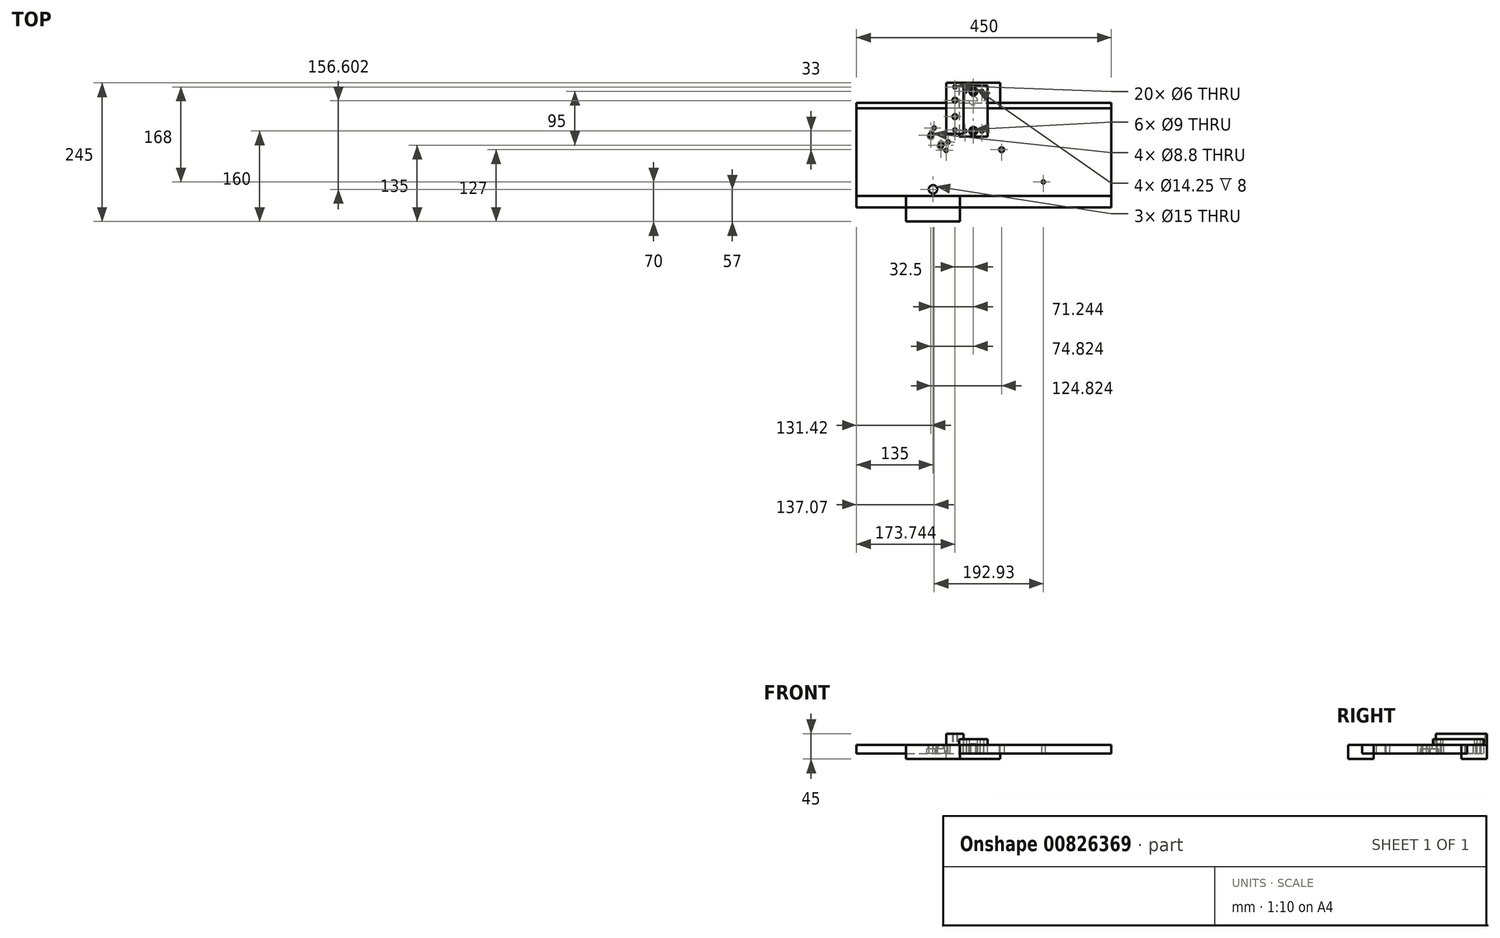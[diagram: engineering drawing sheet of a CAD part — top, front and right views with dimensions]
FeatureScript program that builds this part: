
annotation { "Feature Type Name" : "Feature", "Feature Type Description" : "" }
export const myFeature = defineFeature(function(context is Context, id is Id, definition is map)
    precondition{}
    {
        {
            var Q0;
            Q0=qCreatedBy(makeId("Top.planeOp"),FACE);
            var sketch = newSketch(context, id + "F0", { "sketchPlane" : qUnion([Q0])});
            skLineSegment(sketch, "E0.bottom", {"start": v(120, -25) * mm, "end": v(-330, -25) * mm});
            skLineSegment(sketch, "E0.top", {"start": v(120, 130) * mm, "end": v(-330, 130) * mm});
            skLineSegment(sketch, "E0.left", {"start": v(120, -25) * mm, "end": v(120, 130) * mm});
            skLineSegment(sketch, "E0.right", {"start": v(-330, -25) * mm, "end": v(-330, 130) * mm});
            skSolve(sketch);
        }
        {
            var Q0;
            Q0=makeQuery(id+"F0.imprint","IMPRINT",FACE,{"disambiguationData":[TD([[makeQuery(id+"F0.imprint","IMPRINT",EDGE,{"derivedFrom":sQuery(id+"F0.wireOp",EDGE,"E0.bottom")}),-1.0]])]});
            extrude(context, id + "F1", {"entities" : qUnion([Q0]), "oppositeDirection" : true, "depth" : 15 * mm, "offsetDistance" : 25 * mm});
        }
        {
            var Q0;
            Q0=makeQuery(id+"F1.opExtrude","CAP_FACE",FACE,{"disambiguationData":[OSD([sQuery(id+"F0.wireOp",EDGE,"E0.bottom"),sQuery(id+"F0.wireOp",EDGE,"E0.top"),sQuery(id+"F0.wireOp",EDGE,"E0.left"),sQuery(id+"F0.wireOp",EDGE,"E0.right")])],"isStart":true});
            var sketch = newSketch(context, id + "F2", { "sketchPlane" : qUnion([Q0])});
            skLineSegment(sketch, "E1.bottom", {"start": v(-330, -25) * mm, "end": v(120, -25) * mm});
            skLineSegment(sketch, "E1.top", {"start": v(-330, -45) * mm, "end": v(120, -45) * mm});
            skLineSegment(sketch, "E1.left", {"start": v(-330, -25) * mm, "end": v(-330, -45) * mm});
            skLineSegment(sketch, "E1.right", {"start": v(120, -25) * mm, "end": v(120, -45) * mm});
            skLineSegment(sketch, "E2.bottom", {"start": v(-330, 130) * mm, "end": v(120, 130) * mm});
            skLineSegment(sketch, "E2.top", {"start": v(-330, 140) * mm, "end": v(120, 140) * mm});
            skLineSegment(sketch, "E2.left", {"start": v(-330, 130) * mm, "end": v(-330, 140) * mm});
            skLineSegment(sketch, "E2.right", {"start": v(120, 130) * mm, "end": v(120, 140) * mm});
            skSolve(sketch);
        }
        {
            var Q0;
            Q0=makeQuery(id+"F2.imprint","IMPRINT",FACE,{"disambiguationData":[TD([[makeQuery(id+"F2.imprint","IMPRINT",EDGE,{"derivedFrom":sQuery(id+"F2.wireOp",EDGE,"E1.bottom")}),-1.0]])]});
            var sketch = newSketch(context, id + "F3", { "sketchPlane" : qUnion([Q0])});
            skLineSegment(sketch, "E3.bottom", {"start": v(-242.5, -25) * mm, "end": v(-147.5, -25) * mm});
            skLineSegment(sketch, "E3.top", {"start": v(-242.5, -70) * mm, "end": v(-147.5, -70) * mm});
            skLineSegment(sketch, "E3.left", {"start": v(-242.5, -25) * mm, "end": v(-242.5, -70) * mm});
            skLineSegment(sketch, "E3.right", {"start": v(-147.5, -25) * mm, "end": v(-147.5, -70) * mm});
            skLineSegment(sketch, "E4", {"start": v(-195, -23) * mm, "end": v(-73.76, 47) * mm});
            skLineSegment(sketch, "E5", {"start": v(-123.76, 133.6) * mm, "end": v(-73.76, 47) * mm});
            skSolve(sketch);
        }
        {
            var Q0;
            Q0=makeQuery(id+"F3.imprint","IMPRINT",FACE,{"disambiguationData":[TD([[makeQuery(id+"F3.imprint","IMPRINT",EDGE,{"derivedFrom":makeQuery(id+"F2.imprint","IMPRINT",EDGE,{"derivedFrom":sQuery(id+"F2.wireOp",EDGE,"E2.bottom")})}),1.0]])]});
            var sketch = newSketch(context, id + "F4", { "sketchPlane" : qUnion([Q0])});
            skLineSegment(sketch, "E6.bottom", {"start": v(-242.5, -70) * mm, "end": v(-147.5, -70) * mm});
            skLineSegment(sketch, "E6.top", {"start": v(-242.5, -25) * mm, "end": v(-147.5, -25) * mm});
            skLineSegment(sketch, "E6.left", {"start": v(-242.5, -70) * mm, "end": v(-242.5, -25) * mm});
            skLineSegment(sketch, "E6.right", {"start": v(-147.5, -70) * mm, "end": v(-147.5, -25) * mm});
            skLineSegment(sketch, "E7.bottom", {"start": v(-171.26, 130) * mm, "end": v(-76.26, 130) * mm});
            skLineSegment(sketch, "E7.top", {"start": v(-171.26, 175) * mm, "end": v(-76.26, 175) * mm});
            skLineSegment(sketch, "E7.left", {"start": v(-171.26, 130) * mm, "end": v(-171.26, 175) * mm});
            skLineSegment(sketch, "E7.right", {"start": v(-76.26, 130) * mm, "end": v(-76.26, 175) * mm});
            skSolve(sketch);
        }
        {
            var Q0;
            Q0 = qSketchRegion(id + "F4", true);
            extrude(context, id + "F5", {"entities" : qUnion([Q0]), "oppositeDirection" : true, "depth" : 25 * mm, "offsetDistance" : 25 * mm});
        }
        {
            var Q0;
            Q0=makeQuery(id+"F5.opExtrude","CAP_FACE",FACE,{"disambiguationData":[OSD([sQuery(id+"F4.wireOp",EDGE,"E7.bottom"),sQuery(id+"F4.wireOp",EDGE,"E7.top"),sQuery(id+"F4.wireOp",EDGE,"E7.left"),sQuery(id+"F4.wireOp",EDGE,"E7.right")])],"isStart":true});
            var sketch = newSketch(context, id + "F6", { "sketchPlane" : qUnion([Q0])});
            skLineSegment(sketch, "E8.bottom", {"start": v(-171.26, 175) * mm, "end": v(-141.26, 175) * mm});
            skLineSegment(sketch, "E8.top", {"start": v(-171.26, 85) * mm, "end": v(-141.26, 85) * mm});
            skLineSegment(sketch, "E8.left", {"start": v(-171.26, 175) * mm, "end": v(-171.26, 85) * mm});
            skLineSegment(sketch, "E8.right", {"start": v(-141.26, 175) * mm, "end": v(-141.26, 85) * mm});
            skCircle(sketch, "E9", {"center": v(-156.26, 168) * mm, "radius": 3 * mm});
            skCircle(sketch, "E10", {"center": v(-156.26, 144.5) * mm, "radius": 4.5 * mm});
            skCircle(sketch, "E11", {"center": v(-156.26, 115.5) * mm, "radius": 4.5 * mm});
            skCircle(sketch, "E12", {"center": v(-156.26, 92) * mm, "radius": 3 * mm});
            skLineSegment(sketch, "E13", {"start": v(-156.26, 168) * mm, "end": v(-156.26, 144.5) * mm});
            skLineSegment(sketch, "E14", {"start": v(-156.26, 115.5) * mm, "end": v(-156.26, 92) * mm});
            skLineSegment(sketch, "E15", {"start": v(-156.26, 115.5) * mm, "end": v(-156.26, 144.5) * mm});
            skPoint(sketch, "E16", {"position": v(-156.26, 175) * mm});
            skLineSegment(sketch, "E17", {"start": v(-91.26, 168) * mm, "end": v(-91.26, 144.5) * mm});
            skLineSegment(sketch, "E18", {"start": v(-91.26, 144.5) * mm, "end": v(-91.26, 115.5) * mm});
            skLineSegment(sketch, "E19", {"start": v(-91.26, 115.5) * mm, "end": v(-91.26, 92) * mm});
            skLineSegment(sketch, "E20", {"start": v(-156.26, 168) * mm, "end": v(-91.26, 168) * mm});
            skLineSegment(sketch, "E21", {"start": v(-162.5, -63) * mm, "end": v(-162.5, -39.5) * mm});
            skLineSegment(sketch, "E22", {"start": v(-162.5, -10.5) * mm, "end": v(-162.5, 13) * mm});
            skLineSegment(sketch, "E23", {"start": v(-162.5, -10.5) * mm, "end": v(-162.5, -39.5) * mm});
            skLineSegment(sketch, "E24", {"start": v(-227.5, -63) * mm, "end": v(-227.5, -39.5) * mm});
            skLineSegment(sketch, "E25", {"start": v(-227.5, -39.5) * mm, "end": v(-227.5, -10.5) * mm});
            skLineSegment(sketch, "E26", {"start": v(-227.5, -10.5) * mm, "end": v(-227.5, 13) * mm});
            skLineSegment(sketch, "E27", {"start": v(-162.5, -63) * mm, "end": v(-227.5, -63) * mm});
            skSolve(sketch);
        }
        {
            var Q0;
            Q0 = qSketchRegion(id + "F6", true);
            extrude(context, id + "F7", {"entities" : qUnion([Q0]), "depth" : 20 * mm, "offsetDistance" : 25 * mm});
        }
        {
            var Q0;
            Q0=makeQuery(id+"F2.imprint","IMPRINT",FACE,{"disambiguationData":[TD([[makeQuery(id+"F2.imprint","IMPRINT",EDGE,{"derivedFrom":sQuery(id+"F2.wireOp",EDGE,"E1.bottom")}),-1.0]])]});
            var sketch = newSketch(context, id + "F8", { "sketchPlane" : qUnion([Q0])});
            skLineSegment(sketch, "E28", {"start": v(-192.93, 95.4) * mm, "end": v(-168.18, 70.66) * mm});
            skLineSegment(sketch, "E29", {"start": v(-198.58, 82.68) * mm, "end": v(-180.9, 65) * mm});
            skLineSegment(sketch, "E30", {"start": v(-168.18, 70.66) * mm, "end": v(-171.71, 55.8) * mm});
            skSolve(sketch);
        }
        {
            var Q0;
            Q0=sQuery(id+"F8.wireOp",VERTEX,"E28.start");
            var Q1;
            Q1=sQuery(id+"F8.wireOp",VERTEX,"E28.end");
            var Q2;
            Q2=sQuery(id+"F8.wireOp",VERTEX,"E30.end");
            var Q3;
            Q3=makeQuery(id+"F1.opExtrude","SWEPT_BODY",BODY,{"disambiguationData":[OSD([sQuery(id+"F0.wireOp",EDGE,"E0.bottom"),sQuery(id+"F0.wireOp",EDGE,"E0.top"),sQuery(id+"F0.wireOp",EDGE,"E0.left"),sQuery(id+"F0.wireOp",EDGE,"E0.right")])]});
            hole(context, id + "F9", {"style" : HoleStyle.SIMPLE, "endStyle" : HoleEndStyle.BLIND, "holeDiameter" : 6 * mm, "majorDiameter" : 5 * mm, "holeDepth" : 25 * mm, "isTappedThrough" : true, "tappedDepth" : 12 * mm, "tapClearance" : 3, "locations" : qUnion([Q0, Q1, Q2]), "scope" : qUnion([Q3]), "startStyle" : HoleStartStyle.SKETCH});
        }
        {
            var Q0;
            Q0=makeQuery(id+"F1.opExtrude","CAP_FACE",FACE,{"disambiguationData":[OSD([sQuery(id+"F0.wireOp",EDGE,"E0.bottom"),sQuery(id+"F0.wireOp",EDGE,"E0.top"),sQuery(id+"F0.wireOp",EDGE,"E0.left"),sQuery(id+"F0.wireOp",EDGE,"E0.right")])],"isStart":false});
            var sketch = newSketch(context, id + "F10", { "sketchPlane" : qUnion([Q0])});
            skPoint(sketch, "E31", {"position": v(-198.58, -82.68) * mm});
            skPoint(sketch, "E32", {"position": v(-180.9, -65) * mm});
            skSolve(sketch);
        }
        {
            var Q0;
            Q0=sQuery(id+"F10.wireOp",VERTEX,"E32");
            var Q1;
            Q1=sQuery(id+"F10.wireOp",VERTEX,"E31");
            var Q2;
            Q2=makeQuery(id+"F1.opExtrude","SWEPT_BODY",BODY,{"disambiguationData":[OSD([sQuery(id+"F0.wireOp",EDGE,"E0.bottom"),sQuery(id+"F0.wireOp",EDGE,"E0.top"),sQuery(id+"F0.wireOp",EDGE,"E0.left"),sQuery(id+"F0.wireOp",EDGE,"E0.right")])]});
            hole(context, id + "F11", {"style" : HoleStyle.C_BORE, "endStyle" : HoleEndStyle.BLIND, "standardTappedOrClearance" : lookupTablePath({ "fit" : "Normal", "standard" : "ISO", "size" : "M8", "type" : "Clearance" }), "standardBlindInLast" : lookupTablePath({ "fit" : "Standard", "standard" : "ISO", "size" : "M8", "type" : "Clearance" }), "holeDiameter" : 8.8 * mm, "cBoreDiameter" : 14.25 * mm, "cBoreDepth" : 8 * mm, "majorDiameter" : 5 * mm, "holeDepth" : 25 * mm, "isTappedThrough" : true, "tappedDepth" : 12 * mm, "tapClearance" : 3, "locations" : qUnion([Q0, Q1]), "scope" : qUnion([Q2]), "startStyle" : HoleStartStyle.SKETCH});
        }
        {
            var Q0;
            Q0=makeQuery(id+"F8.imprint","IMPRINT",FACE,{"disambiguationData":[TD([[makeQuery(id+"F8.imprint","IMPRINT",EDGE,{"derivedFrom":makeQuery(id+"F2.imprint","IMPRINT",EDGE,{"derivedFrom":sQuery(id+"F2.wireOp",EDGE,"E1.bottom")})}),-1.0]])]});
            var sketch = newSketch(context, id + "F12", { "sketchPlane" : qUnion([Q0])});
            skLineSegment(sketch, "E33", {"start": v(-123.76, 133.6) * mm, "end": v(-123.76, 143.6) * mm});
            skLineSegment(sketch, "E34", {"start": v(-195, -13) * mm, "end": v(-195, -23) * mm});
            skCircle(sketch, "E35", {"center": v(-195, -13) * mm, "radius": 7.5 * mm});
            skCircle(sketch, "E36", {"center": v(-123.76, 143.6) * mm, "radius": 7.5 * mm});
            skLineSegment(sketch, "E37", {"start": v(-73.76, 47) * mm, "end": v(-73.76, 57) * mm});
            skCircle(sketch, "E38", {"center": v(-73.76, 57) * mm, "radius": 4.5 * mm});
            skSolve(sketch);
        }
        {
            var Q0;
            Q0=makeQuery(id+"F8.imprint","IMPRINT",FACE,{"disambiguationData":[TD([[makeQuery(id+"F8.imprint","IMPRINT",EDGE,{"derivedFrom":makeQuery(id+"F2.imprint","IMPRINT",EDGE,{"derivedFrom":sQuery(id+"F2.wireOp",EDGE,"E1.bottom")})}),-1.0]])]});
            var sketch = newSketch(context, id + "F13", { "sketchPlane" : qUnion([Q0])});
            skLineSegment(sketch, "E39.right", {"start": v(120, -25) * mm, "end": v(120, 130) * mm});
            skLineSegment(sketch, "E40.bottom", {"start": v(-148.76, 130) * mm, "end": v(-98.76, 130) * mm});
            skLineSegment(sketch, "E40.top", {"start": v(-148.76, 170) * mm, "end": v(-98.76, 170) * mm});
            skLineSegment(sketch, "E40.left", {"start": v(-148.76, 130) * mm, "end": v(-148.76, 170) * mm});
            skLineSegment(sketch, "E40.right", {"start": v(-98.76, 130) * mm, "end": v(-98.76, 170) * mm});
            skCircle(sketch, "E41", {"center": v(-123.76, 143.6) * mm, "radius": 7.5 * mm});
            skPoint(sketch, "E42", {"position": v(-123.76, 170) * mm});
            skLineSegment(sketch, "E43", {"start": v(-123.76, 143.6) * mm, "end": v(-123.76, 170) * mm});
            skCircle(sketch, "E44", {"center": v(-108.76, 160) * mm, "radius": 3 * mm});
            skCircle(sketch, "E45", {"center": v(-138.76, 160) * mm, "radius": 3 * mm});
            skCircle(sketch, "E46", {"center": v(-123.76, 160) * mm, "radius": 4.5 * mm});
            skLineSegment(sketch, "E47", {"start": v(-138.76, 160) * mm, "end": v(-123.76, 160) * mm});
            skLineSegment(sketch, "E48", {"start": v(-108.76, 160) * mm, "end": v(-123.76, 160) * mm});
            skSolve(sketch);
        }
        {
            var Q0;
            Q0 = qSketchRegion(id + "F13", true);
            extrude(context, id + "F14", {"entities" : qUnion([Q0]), "oppositeDirection" : true, "depth" : 15 * mm, "offsetDistance" : 25 * mm});
        }
        {
            var Q0;
            Q0=makeQuery(id+"F2.imprint","IMPRINT",FACE,{"disambiguationData":[TD([[makeQuery(id+"F2.imprint","IMPRINT",EDGE,{"derivedFrom":sQuery(id+"F2.wireOp",EDGE,"E1.bottom")}),-1.0]])]});
            var sketch = newSketch(context, id + "F15", { "sketchPlane" : qUnion([Q0])});
            skLineSegment(sketch, "E49.bottom", {"start": v(-148.76, 170) * mm, "end": v(-98.76, 170) * mm});
            skLineSegment(sketch, "E49.top", {"start": v(-148.76, 80) * mm, "end": v(-98.76, 80) * mm});
            skLineSegment(sketch, "E49.left", {"start": v(-148.76, 170) * mm, "end": v(-148.76, 80) * mm});
            skLineSegment(sketch, "E49.right", {"start": v(-98.76, 170) * mm, "end": v(-98.76, 80) * mm});
            skCircle(sketch, "E50", {"center": v(-138.76, 90) * mm, "radius": 3 * mm});
            skCircle(sketch, "E51", {"center": v(-123.76, 90) * mm, "radius": 4.5 * mm});
            skCircle(sketch, "E52", {"center": v(-108.76, 90) * mm, "radius": 3 * mm});
            skLineSegment(sketch, "E53", {"start": v(-138.76, 90) * mm, "end": v(-123.76, 90) * mm});
            skLineSegment(sketch, "E54", {"start": v(-123.76, 90) * mm, "end": v(-108.76, 90) * mm});
            skLineSegment(sketch, "E55", {"start": v(-123.76, 160) * mm, "end": v(-123.76, 90) * mm});
            skLineSegment(sketch, "E56", {"start": v(-138.76, 90) * mm, "end": v(-138.76, 160) * mm});
            skLineSegment(sketch, "E57", {"start": v(-108.76, 90) * mm, "end": v(-108.76, 160) * mm});
            skCircle(sketch, "E58", {"center": v(-138.76, 160) * mm, "radius": 3 * mm});
            skCircle(sketch, "E59", {"center": v(-123.76, 160) * mm, "radius": 4.5 * mm});
            skCircle(sketch, "E60", {"center": v(-108.76, 160) * mm, "radius": 3 * mm});
            skSolve(sketch);
        }
        {
            var Q0;
            Q0 = qSketchRegion(id + "F15", true);
            extrude(context, id + "F16", {"entities" : qUnion([Q0]), "depth" : 10 * mm, "offsetDistance" : 25 * mm});
        }
        {
            var Q0;
            Q0=makeQuery(id+"F16.opExtrude","CAP_FACE",FACE,{"disambiguationData":[OSD([sQuery(id+"F15.wireOp",EDGE,"E49.bottom"),sQuery(id+"F15.wireOp",EDGE,"E49.top"),sQuery(id+"F15.wireOp",EDGE,"E49.left"),sQuery(id+"F15.wireOp",EDGE,"E49.right"),sQuery(id+"F15.wireOp",EDGE,"E50"),sQuery(id+"F15.wireOp",EDGE,"E51"),sQuery(id+"F15.wireOp",EDGE,"E52"),sQuery(id+"F15.wireOp",EDGE,"E58"),sQuery(id+"F15.wireOp",EDGE,"E59"),sQuery(id+"F15.wireOp",EDGE,"E60")])],"isStart":false});
            var sketch = newSketch(context, id + "F17", { "sketchPlane" : qUnion([Q0])});
            skLineSegment(sketch, "E61", {"start": v(-123.76, 90) * mm, "end": v(-123.76, 160) * mm});
            skSolve(sketch);
        }
        {
            var Q0;
            Q0=sQuery(id+"F17.wireOp",VERTEX,"E61.end");
            var Q1;
            Q1=sQuery(id+"F17.wireOp",VERTEX,"E61.start");
            var Q2;
            Q2=makeQuery(id+"F16.opExtrude","SWEPT_BODY",BODY,{"disambiguationData":[OSD([sQuery(id+"F15.wireOp",EDGE,"E49.bottom"),sQuery(id+"F15.wireOp",EDGE,"E49.top"),sQuery(id+"F15.wireOp",EDGE,"E49.left"),sQuery(id+"F15.wireOp",EDGE,"E49.right"),sQuery(id+"F15.wireOp",EDGE,"E50"),sQuery(id+"F15.wireOp",EDGE,"E51"),sQuery(id+"F15.wireOp",EDGE,"E52"),sQuery(id+"F15.wireOp",EDGE,"E58"),sQuery(id+"F15.wireOp",EDGE,"E59"),sQuery(id+"F15.wireOp",EDGE,"E60")])]});
            hole(context, id + "F18", {"style" : HoleStyle.C_BORE, "endStyle" : HoleEndStyle.BLIND, "standardTappedOrClearance" : lookupTablePath({ "fit" : "Normal", "standard" : "ISO", "size" : "M8", "type" : "Clearance" }), "standardBlindInLast" : lookupTablePath({ "fit" : "Standard", "standard" : "ISO", "size" : "M8", "type" : "Clearance" }), "holeDiameter" : 8.8 * mm, "cBoreDiameter" : 14.25 * mm, "cBoreDepth" : 8 * mm, "majorDiameter" : 8 * mm, "holeDepth" : 15.75 * mm, "isTappedThrough" : true, "tappedDepth" : 12 * mm, "tapClearance" : 3, "locations" : qUnion([Q0, Q1]), "scope" : qUnion([Q2]), "startStyle" : HoleStartStyle.SKETCH});
        }
        {
            var Q0;
            Q0=sQuery(id+"F15.wireOp",VERTEX,"E53.end");
            var Q1;
            Q1=makeQuery(id+"F1.opExtrude","SWEPT_BODY",BODY,{"disambiguationData":[OSD([sQuery(id+"F0.wireOp",EDGE,"E0.bottom"),sQuery(id+"F0.wireOp",EDGE,"E0.top"),sQuery(id+"F0.wireOp",EDGE,"E0.left"),sQuery(id+"F0.wireOp",EDGE,"E0.right")])]});
            hole(context, id + "F19", {"style" : HoleStyle.SIMPLE, "endStyle" : HoleEndStyle.BLIND, "standardTappedOrClearance" : lookupTablePath({ "fit" : "Normal", "standard" : "ISO", "size" : "M8", "type" : "Clearance" }), "standardBlindInLast" : lookupTablePath({ "fit" : "Standard", "standard" : "ISO", "size" : "M8", "type" : "Clearance" }), "holeDiameter" : 8.8 * mm, "majorDiameter" : 5 * mm, "holeDepth" : 50 * mm, "isTappedThrough" : true, "tappedDepth" : 12 * mm, "tapClearance" : 3, "locations" : qUnion([Q0]), "scope" : qUnion([Q1]), "startStyle" : HoleStartStyle.SKETCH});
        }
        {
            var Q0;
            Q0=sQuery(id+"F15.wireOp",VERTEX,"E53.start");
            var Q1;
            Q1=sQuery(id+"F15.wireOp",VERTEX,"E54.end");
            var Q2;
            Q2=makeQuery(id+"F1.opExtrude","SWEPT_BODY",BODY,{"disambiguationData":[OSD([sQuery(id+"F0.wireOp",EDGE,"E0.bottom"),sQuery(id+"F0.wireOp",EDGE,"E0.top"),sQuery(id+"F0.wireOp",EDGE,"E0.left"),sQuery(id+"F0.wireOp",EDGE,"E0.right")])]});
            hole(context, id + "F20", {"style" : HoleStyle.SIMPLE, "endStyle" : HoleEndStyle.BLIND, "holeDiameter" : 6 * mm, "majorDiameter" : 5 * mm, "holeDepth" : 50 * mm, "isTappedThrough" : true, "tappedDepth" : 12 * mm, "tapClearance" : 3, "locations" : qUnion([Q0, Q1]), "scope" : qUnion([Q2]), "startStyle" : HoleStartStyle.SKETCH});
        }
        {
            var Q0;
            Q0=sQuery(id+"F12.wireOp",VERTEX,"E37.end");
            var Q1;
            Q1=makeQuery(id+"F1.opExtrude","SWEPT_BODY",BODY,{"disambiguationData":[OSD([sQuery(id+"F0.wireOp",EDGE,"E0.bottom"),sQuery(id+"F0.wireOp",EDGE,"E0.top"),sQuery(id+"F0.wireOp",EDGE,"E0.left"),sQuery(id+"F0.wireOp",EDGE,"E0.right")])]});
            hole(context, id + "F21", {"style" : HoleStyle.SIMPLE, "endStyle" : HoleEndStyle.BLIND, "standardTappedOrClearance" : lookupTablePath({ "fit" : "Normal", "standard" : "ISO", "size" : "M8", "type" : "Clearance" }), "standardBlindInLast" : lookupTablePath({ "fit" : "Standard", "standard" : "ISO", "size" : "M8", "type" : "Clearance" }), "holeDiameter" : 8.8 * mm, "majorDiameter" : 5 * mm, "holeDepth" : 50 * mm, "isTappedThrough" : true, "tappedDepth" : 12 * mm, "tapClearance" : 3, "locations" : qUnion([Q0]), "scope" : qUnion([Q1]), "startStyle" : HoleStartStyle.SKETCH});
        }
        {
            var Q0;
            Q0=sQuery(id+"F12.wireOp",VERTEX,"E34.start");
            var Q1;
            Q1=makeQuery(id+"F1.opExtrude","SWEPT_BODY",BODY,{"disambiguationData":[OSD([sQuery(id+"F0.wireOp",EDGE,"E0.bottom"),sQuery(id+"F0.wireOp",EDGE,"E0.top"),sQuery(id+"F0.wireOp",EDGE,"E0.left"),sQuery(id+"F0.wireOp",EDGE,"E0.right")])]});
            hole(context, id + "F22", {"style" : HoleStyle.SIMPLE, "endStyle" : HoleEndStyle.BLIND, "holeDiameter" : 15 * mm, "majorDiameter" : 5 * mm, "holeDepth" : 50 * mm, "isTappedThrough" : true, "tappedDepth" : 12 * mm, "tapClearance" : 3, "locations" : qUnion([Q0]), "scope" : qUnion([Q1]), "startStyle" : HoleStartStyle.SKETCH});
        }
        {
            var Q0;
            {var subQ2=sQuery(id+"F3.wireOp",EDGE,"E3.bottom");Q0=makeQuery(id+"F3.imprint","IMPRINT",FACE,{"disambiguationData":[TD([[makeQuery(id+"F3.imprint","IMPRINT",EDGE,{"derivedFrom":subQ2}),-1.0]])]});}
            var sketch = newSketch(context, id + "F23", { "sketchPlane" : qUnion([Q0])});
            skLineSegment(sketch, "E62.bottom", {"start": v(-330, 140) * mm, "end": v(120, 140) * mm});
            skLineSegment(sketch, "E62.top", {"start": v(-330, -45) * mm, "end": v(120, -45) * mm});
            skLineSegment(sketch, "E62.left", {"start": v(-330, 140) * mm, "end": v(-330, -45) * mm});
            skLineSegment(sketch, "E62.right", {"start": v(120, 140) * mm, "end": v(120, -45) * mm});
            skLineSegment(sketch, "E63", {"start": v(-195, -23) * mm, "end": v(-73.76, 47) * mm});
            skLineSegment(sketch, "E64", {"start": v(-73.76, 47) * mm, "end": v(-123.76, 133.6) * mm});
            skLineSegment(sketch, "E65", {"start": v(-192.93, 95.4) * mm, "end": v(-168.18, 70.66) * mm});
            skLineSegment(sketch, "E66", {"start": v(-168.18, 70.66) * mm, "end": v(-171.71, 55.8) * mm});
            skLineSegment(sketch, "E67", {"start": v(-198.58, 82.68) * mm, "end": v(-180.9, 65) * mm});
            skSolve(sketch);
        }
        {
            var Q0;
            Q0 = qSketchRegion(id + "F23", true);
            extrude(context, id + "F24", {"entities" : qUnion([Q0]), "oppositeDirection" : true, "depth" : 15 * mm, "offsetDistance" : 25 * mm});
        }
        {
            var Q0;
            Q0=sQuery(id+"F8.wireOp",VERTEX,"E28.start");
            var Q1;
            Q1=sQuery(id+"F8.wireOp",VERTEX,"E28.end");
            var Q2;
            Q2=sQuery(id+"F8.wireOp",VERTEX,"E30.end");
            var Q3;
            Q3=makeQuery(id+"F24.opExtrude","SWEPT_BODY",BODY,{"disambiguationData":[OSD([sQuery(id+"F23.wireOp",EDGE,"E62.bottom"),sQuery(id+"F23.wireOp",EDGE,"E62.top"),sQuery(id+"F23.wireOp",EDGE,"E62.left"),sQuery(id+"F23.wireOp",EDGE,"E62.right")])]});
            hole(context, id + "F25", {"style" : HoleStyle.SIMPLE, "endStyle" : HoleEndStyle.BLIND, "holeDiameter" : 6 * mm, "majorDiameter" : 5 * mm, "holeDepth" : 50 * mm, "isTappedThrough" : true, "tappedDepth" : 12 * mm, "tapClearance" : 3, "locations" : qUnion([Q0, Q1, Q2]), "scope" : qUnion([Q3]), "startStyle" : HoleStartStyle.SKETCH});
        }
        {
            var Q0;
            Q0=makeQuery(id+"F24.opExtrude","CAP_FACE",FACE,{"disambiguationData":[OSD([sQuery(id+"F23.wireOp",EDGE,"E62.bottom"),sQuery(id+"F23.wireOp",EDGE,"E62.top"),sQuery(id+"F23.wireOp",EDGE,"E62.left"),sQuery(id+"F23.wireOp",EDGE,"E62.right")])],"isStart":true});
            var sketch = newSketch(context, id + "F26", { "sketchPlane" : qUnion([Q0])});
            skPoint(sketch, "E68", {"position": v(0, 0) * mm});
            skSolve(sketch);
        }
        {
            var Q0;
            Q0=sQuery(id+"F26.wireOp",VERTEX,"E68");
            var Q1;
            Q1=makeQuery(id+"F1.opExtrude","SWEPT_BODY",BODY,{"disambiguationData":[OSD([sQuery(id+"F0.wireOp",EDGE,"E0.bottom"),sQuery(id+"F0.wireOp",EDGE,"E0.top"),sQuery(id+"F0.wireOp",EDGE,"E0.left"),sQuery(id+"F0.wireOp",EDGE,"E0.right")])]});
            var Q2;
            Q2=makeQuery(id+"F24.opExtrude","SWEPT_BODY",BODY,{"disambiguationData":[OSD([sQuery(id+"F23.wireOp",EDGE,"E62.bottom"),sQuery(id+"F23.wireOp",EDGE,"E62.top"),sQuery(id+"F23.wireOp",EDGE,"E62.left"),sQuery(id+"F23.wireOp",EDGE,"E62.right")])]});
            hole(context, id + "F27", {"style" : HoleStyle.SIMPLE, "endStyle" : HoleEndStyle.BLIND, "holeDiameter" : 6 * mm, "majorDiameter" : 5 * mm, "holeDepth" : 50 * mm, "isTappedThrough" : true, "tappedDepth" : 12 * mm, "tapClearance" : 3, "locations" : qUnion([Q0]), "scope" : qUnion([Q1, Q2]), "startStyle" : HoleStartStyle.SKETCH});
        }
        {
            var Q0;
            Q0=sQuery(id+"F12.wireOp",VERTEX,"E33.end");
            var Q1;
            Q1=makeQuery(id+"F5.opExtrude","SWEPT_BODY",BODY,{"disambiguationData":[OSD([sQuery(id+"F4.wireOp",EDGE,"E7.bottom"),sQuery(id+"F4.wireOp",EDGE,"E7.top"),sQuery(id+"F4.wireOp",EDGE,"E7.left"),sQuery(id+"F4.wireOp",EDGE,"E7.right")])]});
            hole(context, id + "F28", {"style" : HoleStyle.SIMPLE, "endStyle" : HoleEndStyle.BLIND, "holeDiameter" : 15 * mm, "majorDiameter" : 5 * mm, "holeDepth" : 50 * mm, "isTappedThrough" : true, "tappedDepth" : 12 * mm, "tapClearance" : 3, "locations" : qUnion([Q0]), "scope" : qUnion([Q1]), "startStyle" : HoleStartStyle.SKETCH});
        }
        {
            var Q0;
            Q0=sQuery(id+"F13.wireOp",VERTEX,"E48.start");
            var Q1;
            Q1=sQuery(id+"F13.wireOp",VERTEX,"E47.start");
            var Q2;
            Q2=sQuery(id+"F15.wireOp",VERTEX,"E53.start");
            var Q3;
            Q3=sQuery(id+"F15.wireOp",VERTEX,"E54.end");
            var Q4;
            Q4=makeQuery(id+"F5.opExtrude","SWEPT_BODY",BODY,{"disambiguationData":[OSD([sQuery(id+"F4.wireOp",EDGE,"E7.bottom"),sQuery(id+"F4.wireOp",EDGE,"E7.top"),sQuery(id+"F4.wireOp",EDGE,"E7.left"),sQuery(id+"F4.wireOp",EDGE,"E7.right")])]});
            var Q5;
            Q5=makeQuery(id+"F1.opExtrude","SWEPT_BODY",BODY,{"disambiguationData":[OSD([sQuery(id+"F0.wireOp",EDGE,"E0.bottom"),sQuery(id+"F0.wireOp",EDGE,"E0.top"),sQuery(id+"F0.wireOp",EDGE,"E0.left"),sQuery(id+"F0.wireOp",EDGE,"E0.right")])]});
            hole(context, id + "F29", {"style" : HoleStyle.SIMPLE, "endStyle" : HoleEndStyle.BLIND, "holeDiameter" : 6 * mm, "majorDiameter" : 5 * mm, "holeDepth" : 50 * mm, "isTappedThrough" : true, "tappedDepth" : 12 * mm, "tapClearance" : 3, "locations" : qUnion([Q0, Q1, Q2, Q3]), "scope" : qUnion([Q4, Q5]), "startStyle" : HoleStartStyle.SKETCH});
        }
        {
            var Q0;
            Q0=sQuery(id+"F13.wireOp",VERTEX,"E47.end");
            var Q1;
            Q1=makeQuery(id+"F5.opExtrude","SWEPT_BODY",BODY,{"disambiguationData":[OSD([sQuery(id+"F4.wireOp",EDGE,"E7.bottom"),sQuery(id+"F4.wireOp",EDGE,"E7.top"),sQuery(id+"F4.wireOp",EDGE,"E7.left"),sQuery(id+"F4.wireOp",EDGE,"E7.right")])]});
            hole(context, id + "F30", {"style" : HoleStyle.SIMPLE, "endStyle" : HoleEndStyle.BLIND, "holeDiameter" : 9 * mm, "majorDiameter" : 5 * mm, "holeDepth" : 50 * mm, "isTappedThrough" : true, "tappedDepth" : 12 * mm, "tapClearance" : 3, "locations" : qUnion([Q0]), "scope" : qUnion([Q1]), "startStyle" : HoleStartStyle.SKETCH});
        }
    });
